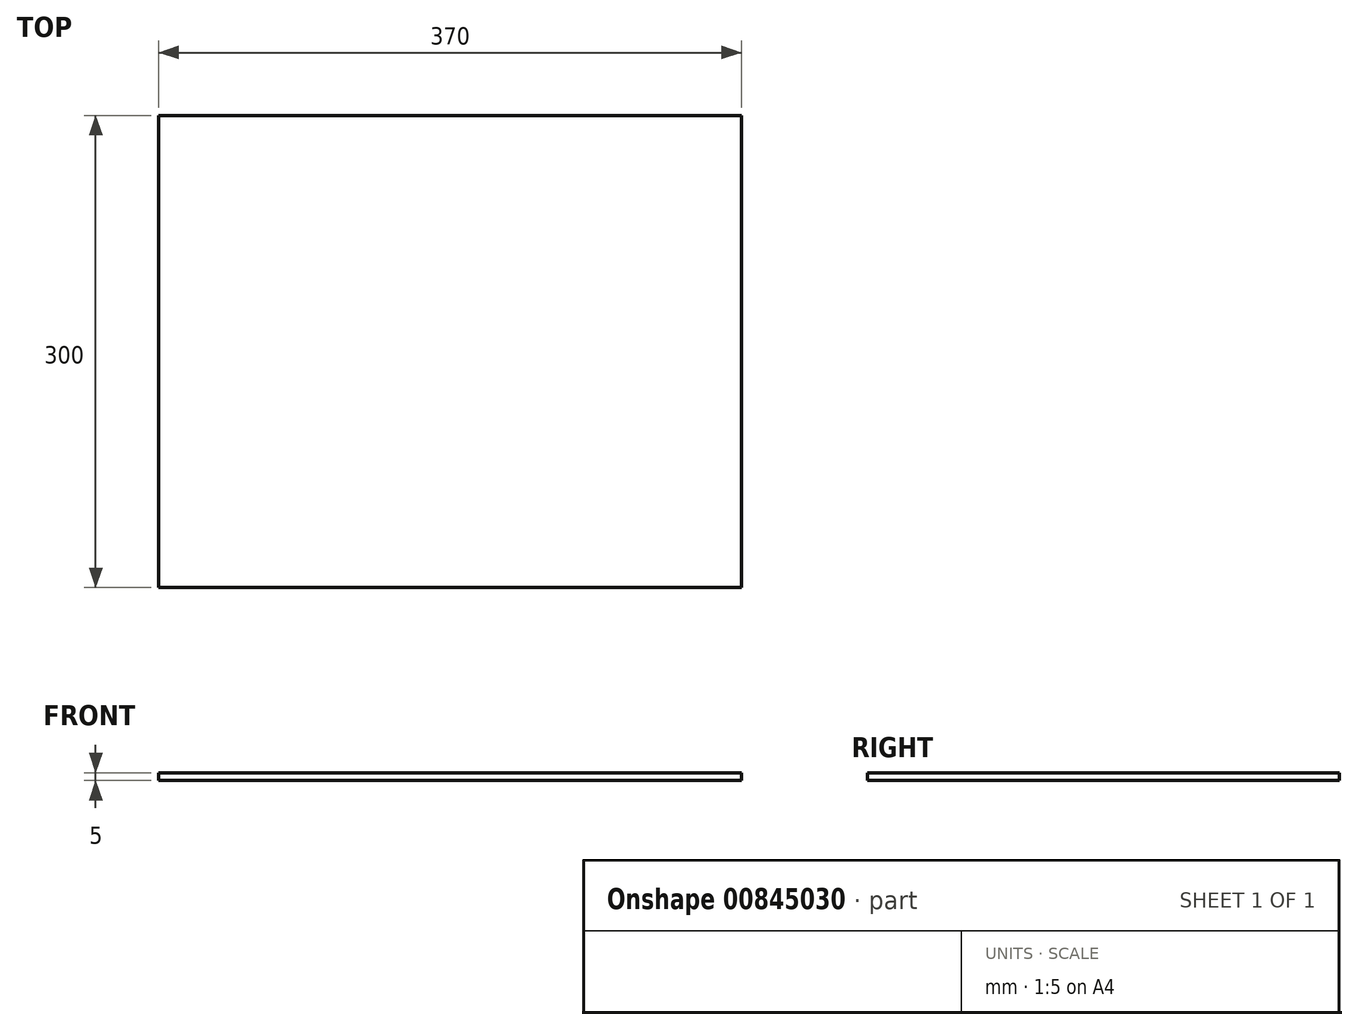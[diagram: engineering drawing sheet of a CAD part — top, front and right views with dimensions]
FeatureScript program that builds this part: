
annotation { "Feature Type Name" : "Feature", "Feature Type Description" : "" }
export const myFeature = defineFeature(function(context is Context, id is Id, definition is map)
    precondition{}
    {
        {
            var Q0;
            Q0=qCreatedBy(makeId("Top.planeOp"),FACE);
            var sketch = newSketch(context, id + "F0", { "sketchPlane" : qUnion([Q0])});
            skLineSegment(sketch, "E0.bottom", {"start": v(-185, 150) * mm, "end": v(185, 150) * mm});
            skLineSegment(sketch, "E0.top", {"start": v(-185, -150) * mm, "end": v(185, -150) * mm});
            skLineSegment(sketch, "E0.left", {"start": v(-185, 150) * mm, "end": v(-185, -150) * mm});
            skLineSegment(sketch, "E0.right", {"start": v(185, 150) * mm, "end": v(185, -150) * mm});
            skPoint(sketch, "E0.middle", {"position": v(0, 0) * mm});
            skSolve(sketch);
        }
        {
            var Q0;
            Q0=makeQuery(id+"F0.imprint","IMPRINT",FACE,{"disambiguationData":[TD([[makeQuery(id+"F0.imprint","IMPRINT",EDGE,{"derivedFrom":sQuery(id+"F0.wireOp",EDGE,"E0.bottom")}),-1.0]])]});
            extrude(context, id + "F1", {"entities" : qUnion([Q0]), "depth" : 5 * mm, "offsetDistance" : 25 * mm});
        }
    });
